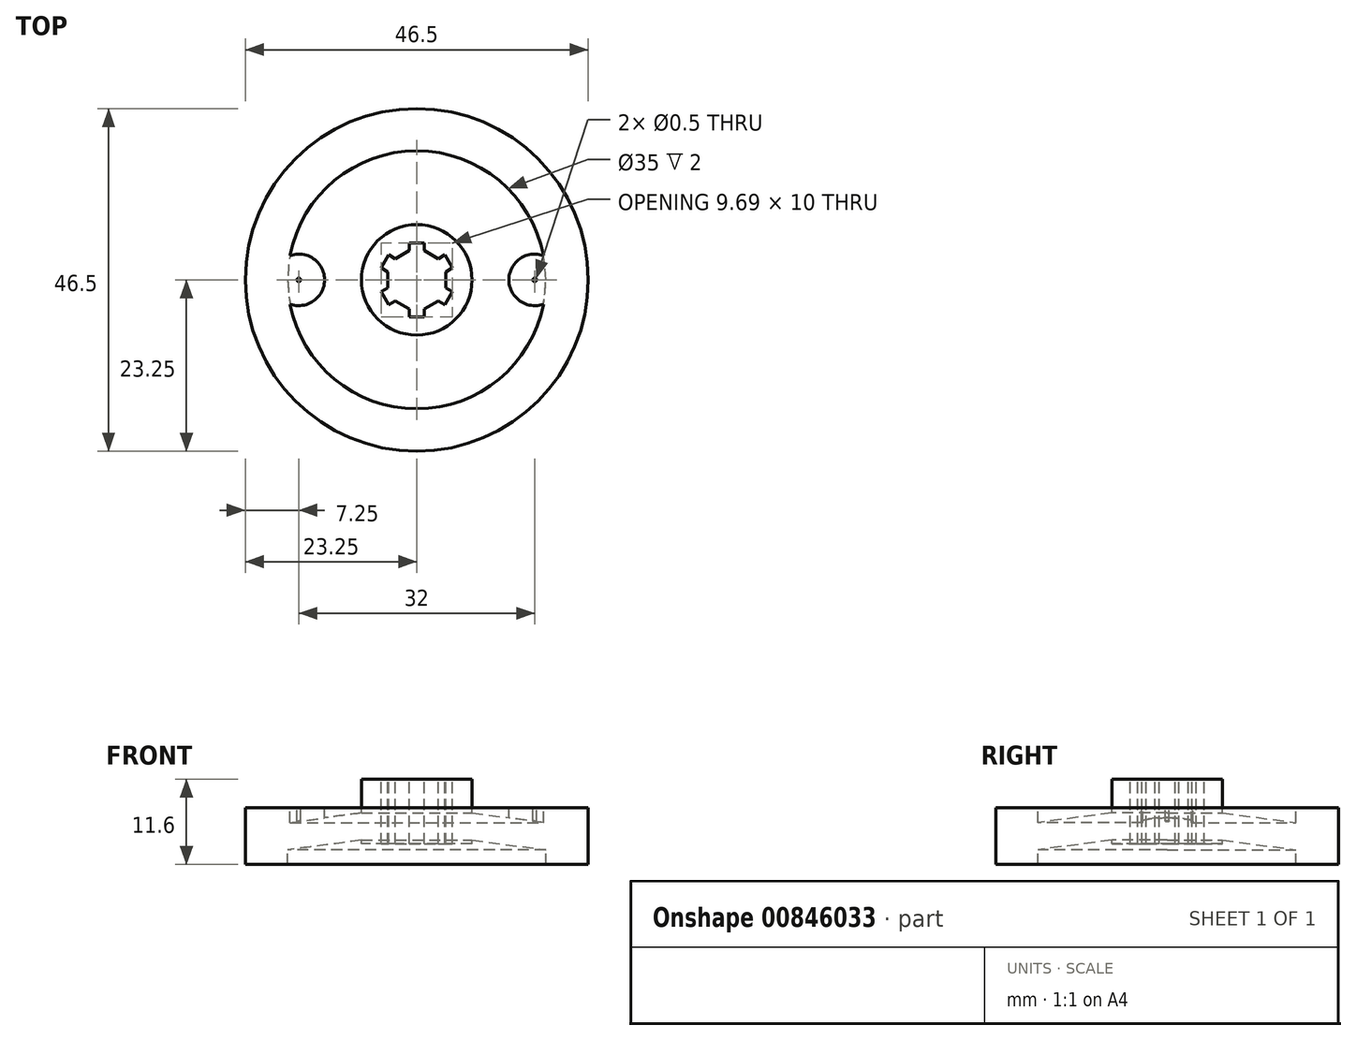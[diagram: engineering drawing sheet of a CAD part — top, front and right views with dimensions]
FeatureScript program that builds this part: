
annotation { "Feature Type Name" : "Feature", "Feature Type Description" : "" }
export const myFeature = defineFeature(function(context is Context, id is Id, definition is map)
    precondition{}
    {
        {
            var Q0;
            Q0=qCreatedBy(makeId("Top.planeOp"),FACE);
            var sketch = newSketch(context, id + "F0", { "sketchPlane" : qUnion([Q0])});
            skCircle(sketch, "E0", {"center": v(0, 0) * mm, "radius": 23.25 * mm});
            skSolve(sketch);
        }
        {
            var Q0;
            Q0 = qSketchRegion(id + "F0", true);
            extrude(context, id + "F1", {"entities" : qUnion([Q0]), "depth" : 7.7 * mm, "offsetDistance" : 25 * mm});
        }
        {
            var Q0;
            Q0=qCreatedBy(makeId("Front.planeOp"),FACE);
            var sketch = newSketch(context, id + "F2", { "sketchPlane" : qUnion([Q0])});
            skLineSegment(sketch, "E1", {"start": v(23.25, 7.7) * mm, "end": v(23.25, 0) * mm});
            skLineSegment(sketch, "E2.0", {"start": v(-23.25, 7.7) * mm, "end": v(23.25, 7.7) * mm, "construction": true});
            skLineSegment(sketch, "E3.0", {"start": v(-23.25, 0) * mm, "end": v(23.25, 0) * mm, "construction": true});
            skLineSegment(sketch, "E4", {"start": v(7.5, 11.6) * mm, "end": v(7.5, 7) * mm, "construction": true});
            skLineSegment(sketch, "E5", {"start": v(17.5, 11.6) * mm, "end": v(7.5, 11.6) * mm});
            skLineSegment(sketch, "E6", {"start": v(0, -2.84) * mm, "end": v(17.5, -2.84) * mm});
            skLineSegment(sketch, "E7", {"start": v(17.5, 2) * mm, "end": v(0, 4.27) * mm});
            skLineSegment(sketch, "E8", {"start": v(17.5, 2) * mm, "end": v(17.5, -2.84) * mm});
            skLineSegment(sketch, "E9", {"start": v(17.5, 11.6) * mm, "end": v(17.5, 5.7) * mm});
            skLineSegment(sketch, "E10", {"start": v(7.5, 11.6) * mm, "end": v(-7.5, 11.6) * mm});
            skPoint(sketch, "E11", {"position": v(0, 11.6) * mm});
            skLineSegment(sketch, "E12", {"start": v(17.5, 11.6) * mm, "end": v(-17.5, 11.6) * mm, "construction": true});
            skLineSegment(sketch, "E13", {"start": v(0, 0) * mm, "end": v(0, 11.6) * mm});
            skLineSegment(sketch, "E14", {"start": v(17.5, 5.7) * mm, "end": v(0, 7.97) * mm});
            skLineSegment(sketch, "E15", {"start": v(0, 0) * mm, "end": v(0, -2.84) * mm});
            skSolve(sketch);
        }
        {
            var Q0;
            {var subQ4=sQuery(id+"F2.wireOp",EDGE,"E5");Q0=makeQuery(id+"F2.imprint","IMPRINT",FACE,{"disambiguationData":[TD([[makeQuery(id+"F2.imprint","IMPRINT",EDGE,{"derivedFrom":subQ4}),1.0]])]});}
            var Q1;
            Q1=makeQuery(id+"F2.imprint","IMPRINT",FACE,{"disambiguationData":[TD([[makeQuery(id+"F2.imprint","IMPRINT",EDGE,{"derivedFrom":sQuery(id+"F2.wireOp",EDGE,"E6")}),1.0]])]});
            var Q2;
            Q2=sQuery(id+"F2.wireOp",EDGE,"E13");
            revolve(context, id + "F3", {"operationType" : NewBodyOperationType.REMOVE, "surfaceOperationType" : NewSurfaceOperationType.NEW, "entities" : qUnion([Q0, Q1]), "axis" : qUnion([Q2]), "revolveType" : RevolveType.FULL, "oppositeDirection" : true});
        }
        {
            var Q0;
            Q0=qCreatedBy(makeId("Top.planeOp"),FACE);
            cPlane(context, id + "F4", {"entities" : qUnion([Q0]), "cplaneType" : CPlaneType.OFFSET, "offset" : 11.6 * mm, "width" : 150 * mm, "height" : 150 * mm});
        }
        {
            var Q0;
            Q0=qCreatedBy(id+"F4.planeOp",FACE);
            var sketch = newSketch(context, id + "F5", { "sketchPlane" : qUnion([Q0])});
            skCircle(sketch, "E16", {"center": v(0, 0) * mm, "radius": 7.5 * mm});
            skSolve(sketch);
        }
        {
            var Q0;
            Q0 = qSketchRegion(id + "F5", true);
            extrude(context, id + "F6", {"entities" : qUnion([Q0]), "operationType" : NewBodyOperationType.ADD, "oppositeDirection" : true, "depth" : 8.8 * mm, "offsetDistance" : 25 * mm});
        }
        {
            var Q0;
            Q0=qCreatedBy(id+"F4.planeOp",FACE);
            var sketch = newSketch(context, id + "F7", { "sketchPlane" : qUnion([Q0])});
            skCircle(sketch, "E17", {"center": v(0, 0) * mm, "radius": 5 * mm, "construction": true});
            skCircle(sketch, "E18.cCircle", {"center": v(0, 0) * mm, "radius": 3.95 * mm, "construction": true});
            skLineSegment(sketch, "E18.0", {"start": v(0, 4.56) * mm, "end": v(3.95, 2.28) * mm});
            skLineSegment(sketch, "E18.1", {"start": v(3.95, 2.28) * mm, "end": v(3.95, -2.28) * mm});
            skLineSegment(sketch, "E18.2", {"start": v(3.95, -2.28) * mm, "end": v(0, -4.56) * mm});
            skLineSegment(sketch, "E18.3", {"start": v(0, -4.56) * mm, "end": v(-3.95, -2.28) * mm});
            skLineSegment(sketch, "E18.4", {"start": v(-3.95, -2.28) * mm, "end": v(-3.95, 2.28) * mm});
            skLineSegment(sketch, "E18.5", {"start": v(-3.95, 2.28) * mm, "end": v(0, 4.56) * mm});
            skPoint(sketch, "E18.0.midPoint", {"position": v(1.97, 3.42) * mm});
            skLineSegment(sketch, "E19.bottom", {"start": v(-1.03, 3.97) * mm, "end": v(1.03, 3.97) * mm, "construction": true});
            skLineSegment(sketch, "E19.top", {"start": v(-1.03, 5) * mm, "end": v(1.03, 5) * mm});
            skLineSegment(sketch, "E19.left", {"start": v(-1.03, 3.97) * mm, "end": v(-1.03, 5) * mm});
            skLineSegment(sketch, "E19.right", {"start": v(1.02, 3.97) * mm, "end": v(1.02, 5) * mm});
            skPoint(sketch, "E20", {"position": v(0, 5) * mm});
            skPoint(sketch, "E21.1.0", {"position": v(-4.33, 2.5) * mm});
            skLineSegment(sketch, "E21.1.1", {"start": v(-4.84, 1.61) * mm, "end": v(-3.82, 3.39) * mm});
            skLineSegment(sketch, "E21.1.2", {"start": v(-2.93, 2.87) * mm, "end": v(-3.82, 3.39) * mm});
            skLineSegment(sketch, "E21.1.3", {"start": v(-3.95, 1.1) * mm, "end": v(-4.84, 1.61) * mm});
            skPoint(sketch, "E21.2.0", {"position": v(-4.33, -2.5) * mm});
            skLineSegment(sketch, "E21.2.1", {"start": v(-3.82, -3.39) * mm, "end": v(-4.84, -1.61) * mm});
            skLineSegment(sketch, "E21.2.2", {"start": v(-3.95, -1.1) * mm, "end": v(-4.84, -1.61) * mm});
            skLineSegment(sketch, "E21.2.3", {"start": v(-2.93, -2.87) * mm, "end": v(-3.82, -3.39) * mm});
            skPoint(sketch, "E21.3.0", {"position": v(0, -5) * mm});
            skLineSegment(sketch, "E21.3.1", {"start": v(1.02, -5) * mm, "end": v(-1.02, -5) * mm});
            skLineSegment(sketch, "E21.3.2", {"start": v(-1.03, -3.97) * mm, "end": v(-1.02, -5) * mm});
            skLineSegment(sketch, "E21.3.3", {"start": v(1.02, -3.97) * mm, "end": v(1.02, -5) * mm});
            skPoint(sketch, "E21.4.0", {"position": v(4.33, -2.5) * mm});
            skLineSegment(sketch, "E21.4.1", {"start": v(4.84, -1.61) * mm, "end": v(3.82, -3.39) * mm});
            skLineSegment(sketch, "E21.4.2", {"start": v(2.92, -2.87) * mm, "end": v(3.82, -3.39) * mm});
            skLineSegment(sketch, "E21.4.3", {"start": v(3.95, -1.1) * mm, "end": v(4.84, -1.61) * mm});
            skPoint(sketch, "E21.5.0", {"position": v(4.33, 2.5) * mm});
            skLineSegment(sketch, "E21.5.1", {"start": v(3.82, 3.39) * mm, "end": v(4.84, 1.61) * mm});
            skLineSegment(sketch, "E21.5.2", {"start": v(3.95, 1.1) * mm, "end": v(4.84, 1.61) * mm});
            skLineSegment(sketch, "E21.5.3", {"start": v(2.93, 2.87) * mm, "end": v(3.82, 3.39) * mm});
            skSolve(sketch);
        }
        {
            var Q0;
            {var subQ10=sQuery(id+"F7.wireOp",EDGE,"E18.5");var subQ11=sQuery(id+"F7.wireOp",EDGE,"E18.0");var subQ12=makeQuery(id+"F7.imprint","INTERSECT",VERTEX,{"derivedFrom":[subQ11,subQ10]});Q0=makeQuery(id+"F7.imprint","IMPRINT",FACE,{"disambiguationData":[TD([[makeQuery(id+"F7.imprint","IMPRINT",EDGE,{"disambiguationData":[TD([[subQ12,-1.0]])],"derivedFrom":subQ11}),-1.0]])]});}
            var Q1;
            Q1=makeQuery(id+"F7.imprint","IMPRINT",FACE,{"disambiguationData":[TD([[makeQuery(id+"F7.imprint","IMPRINT",EDGE,{"derivedFrom":sQuery(id+"F7.wireOp",EDGE,"E19.top")}),-1.0]])]});
            var Q2;
            Q2=makeQuery(id+"F7.imprint","IMPRINT",FACE,{"disambiguationData":[TD([[makeQuery(id+"F7.imprint","IMPRINT",EDGE,{"derivedFrom":sQuery(id+"F7.wireOp",EDGE,"E21.5.1")}),-1.0]])]});
            var Q3;
            Q3=makeQuery(id+"F7.imprint","IMPRINT",FACE,{"disambiguationData":[TD([[makeQuery(id+"F7.imprint","IMPRINT",EDGE,{"derivedFrom":sQuery(id+"F7.wireOp",EDGE,"E21.4.1")}),-1.0]])]});
            var Q4;
            Q4=makeQuery(id+"F7.imprint","IMPRINT",FACE,{"disambiguationData":[TD([[makeQuery(id+"F7.imprint","IMPRINT",EDGE,{"derivedFrom":sQuery(id+"F7.wireOp",EDGE,"E21.3.1")}),-1.0]])]});
            var Q5;
            Q5=makeQuery(id+"F7.imprint","IMPRINT",FACE,{"disambiguationData":[TD([[makeQuery(id+"F7.imprint","IMPRINT",EDGE,{"derivedFrom":sQuery(id+"F7.wireOp",EDGE,"E21.2.1")}),-1.0]])]});
            var Q6;
            Q6=makeQuery(id+"F7.imprint","IMPRINT",FACE,{"disambiguationData":[TD([[makeQuery(id+"F7.imprint","IMPRINT",EDGE,{"derivedFrom":sQuery(id+"F7.wireOp",EDGE,"E21.1.1")}),-1.0]])]});
            var Q7;
            Q7=sQuery(id+"F7.wireOp",EDGE,"E17");
            var Q8;
            Q8=sQuery(id+"F7.wireOp",EDGE,"6skP8rKX-rr0I-vOJd-uh5y-weAJd1akTmno");
            var Q9;
            Q9=sQuery(id+"F7.wireOp",EDGE,"mikZoqVA-AE0s-Q3fu-CLtj-frDffYQYuMXI");
            var Q10;
            Q10=sQuery(id+"F7.wireOp",EDGE,"E18.0");
            extrude(context, id + "F8", {"entities" : qUnion([Q0, Q1, Q2, Q3, Q4, Q5, Q6]), "operationType" : NewBodyOperationType.REMOVE, "surfaceEntities" : qUnion([Q7, Q8, Q9, Q10]), "endBound" : BoundingType.THROUGH_ALL, "oppositeDirection" : true, "depth" : 8.8 * mm, "offsetDistance" : 25 * mm});
        }
        {
            var Q0;
            {var subQ0=sQuery(id+"F0.wireOp",EDGE,"E0");Q0=makeQuery(id+"F3.boolean.opBoolean","SPLIT",FACE,{"disambiguationData":[TD([makeQuery(id+"F1.opExtrude","SWEPT_FACE",FACE,{"disambiguationData":[OSD([subQ0])]})])],"derivedFrom":makeQuery(id+"F1.opExtrude","CAP_FACE",FACE,{"disambiguationData":[OSD([subQ0])],"isStart":false})});}
            var sketch = newSketch(context, id + "F9", { "sketchPlane" : qUnion([Q0])});
            skLineSegment(sketch, "E22", {"start": v(-16, 0) * mm, "end": v(16, 0) * mm});
            skPoint(sketch, "E23", {"position": v(0, 0) * mm});
            skCircle(sketch, "E24", {"center": v(-16, 0) * mm, "radius": 3.5 * mm});
            skCircle(sketch, "E25", {"center": v(16, 0) * mm, "radius": 3.5 * mm});
            skCircle(sketch, "E26", {"center": v(-16, 0) * mm, "radius": 0.25 * mm});
            skCircle(sketch, "E27", {"center": v(16, 0) * mm, "radius": 0.25 * mm});
            skSolve(sketch);
        }
        {
            var Q0;
            Q0 = qSketchRegion(id + "F9", true);
            var Q1;
            Q1=makeQuery(id+"F3.boolean.opBoolean","COPY",FACE,{"derivedFrom":makeQuery(id+"F3.opRevolve","SWEPT_FACE",FACE,{"disambiguationData":[OSD([sQuery(id+"F2.wireOp",EDGE,"E14")])]})});
            extrude(context, id + "F10", {"entities" : qUnion([Q0]), "operationType" : NewBodyOperationType.ADD, "endBound" : BoundingType.UP_TO_SURFACE, "oppositeDirection" : true, "depth" : 25 * mm, "endBoundEntityFace" : qUnion([Q1]), "offsetDistance" : 25 * mm});
        }
    });
